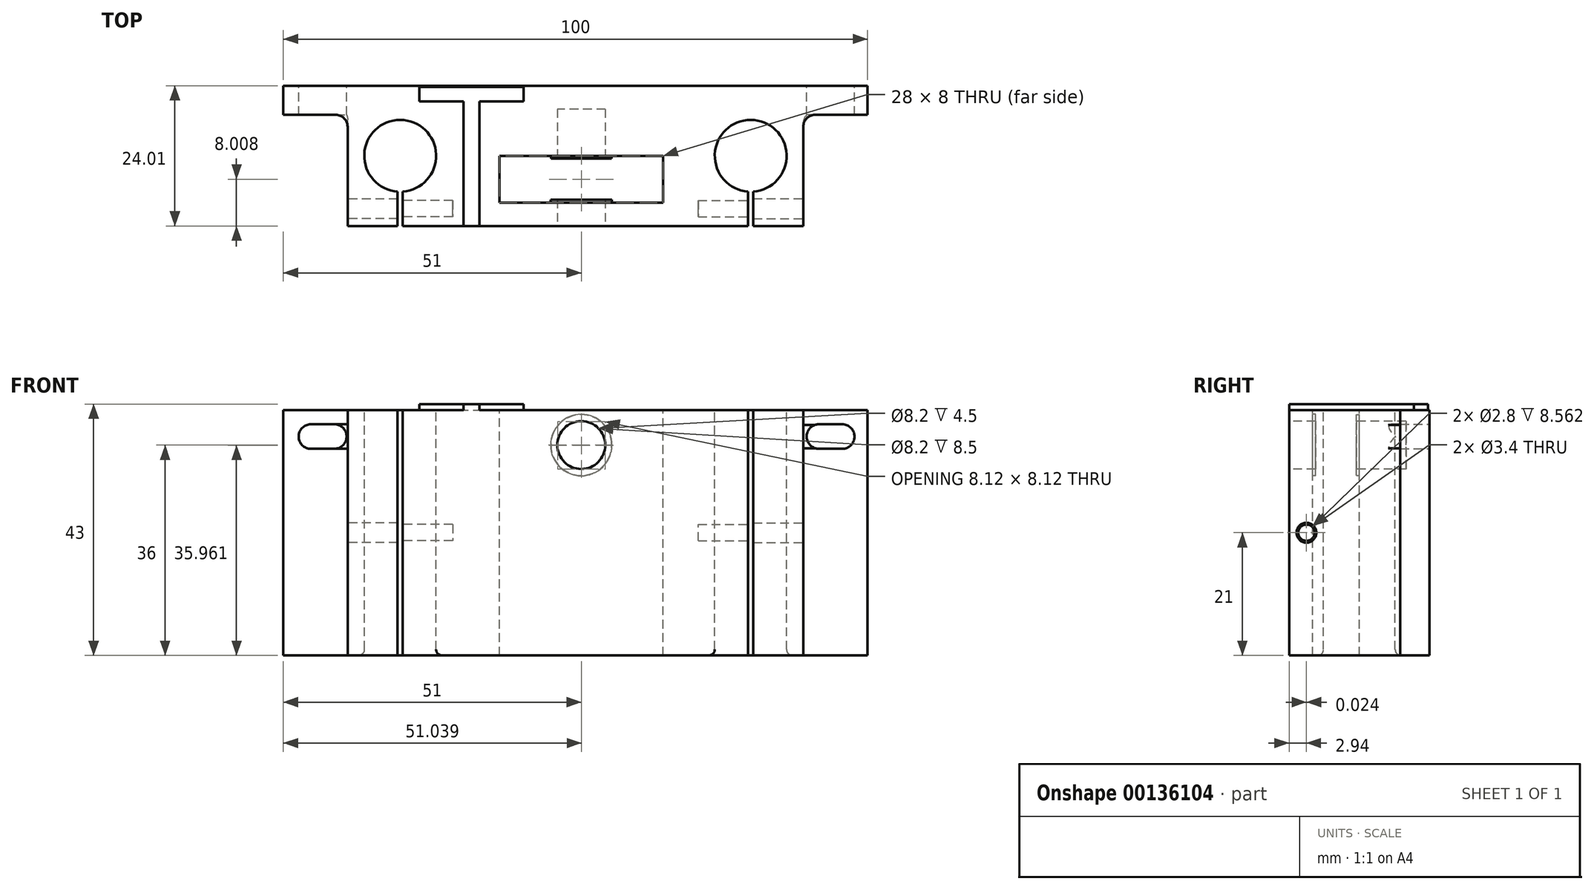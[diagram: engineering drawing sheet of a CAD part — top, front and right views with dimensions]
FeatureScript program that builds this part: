
annotation { "Feature Type Name" : "Feature", "Feature Type Description" : "" }
export const myFeature = defineFeature(function(context is Context, id is Id, definition is map)
    precondition{}
    {
        {
            var Q0;
            Q0=qCreatedBy(makeId("Top.planeOp"),FACE);
            var sketch = newSketch(context, id + "F0", { "sketchPlane" : qUnion([Q0])});
            skLineSegment(sketch, "E0", {"start": v(-46.35, 12.3) * mm, "end": v(53.65, 12.3) * mm});
            skLineSegment(sketch, "E1", {"start": v(53.65, 12.3) * mm, "end": v(53.65, 7.3) * mm});
            skLineSegment(sketch, "E2", {"start": v(53.65, 7.3) * mm, "end": v(42.65, 7.3) * mm});
            skLineSegment(sketch, "E3", {"start": v(42.65, 7.3) * mm, "end": v(42.65, -11.7) * mm});
            skLineSegment(sketch, "E4", {"start": v(42.65, -11.7) * mm, "end": v(-35.35, -11.7) * mm});
            skLineSegment(sketch, "E5", {"start": v(-35.35, -11.7) * mm, "end": v(-35.35, 7.3) * mm});
            skLineSegment(sketch, "E6", {"start": v(-35.35, 7.3) * mm, "end": v(-46.35, 7.3) * mm});
            skLineSegment(sketch, "E7", {"start": v(-46.35, 7.3) * mm, "end": v(-46.35, 12.3) * mm});
            skSolve(sketch);
        }
        {
            var Q0;
            Q0=qSketchRegion(id+"F0",true);
            extrude(context, id + "F1", {"entities" : qUnion([Q0]), "depth" : 12 * mm});
        }
        {
            var Q0;
            Q0=makeQuery(id+"F1.opExtrude","CAP_FACE",FACE,{"disambiguationData":[OSD([sQuery(id+"F0.wireOp",EDGE,"E0"),sQuery(id+"F0.wireOp",EDGE,"E1"),sQuery(id+"F0.wireOp",EDGE,"E2"),sQuery(id+"F0.wireOp",EDGE,"E3"),sQuery(id+"F0.wireOp",EDGE,"E4"),sQuery(id+"F0.wireOp",EDGE,"E5"),sQuery(id+"F0.wireOp",EDGE,"E6"),sQuery(id+"F0.wireOp",EDGE,"E7")])],"isStart":false});
            var sketch = newSketch(context, id + "F2", { "sketchPlane" : qUnion([Q0])});
            skCircle(sketch, "E8", {"center": v(-26.35, 0.3) * mm, "radius": 6.15 * mm});
            skCircle(sketch, "E9", {"center": v(33.65, 0.3) * mm, "radius": 6.15 * mm});
            skPoint(sketch, "E10", {"position": v(3.65, 12.3) * mm});
            skLineSegment(sketch, "E11.bottom", {"start": v(33.21, -3.01) * mm, "end": v(34.09, -3.01) * mm});
            skLineSegment(sketch, "E11.top", {"start": v(33.21, -12.27) * mm, "end": v(34.09, -12.27) * mm});
            skLineSegment(sketch, "E11.left", {"start": v(33.21, -3.01) * mm, "end": v(33.21, -12.27) * mm});
            skLineSegment(sketch, "E11.right", {"start": v(34.09, -3.01) * mm, "end": v(34.09, -12.27) * mm});
            skPoint(sketch, "E12", {"position": v(33.65, -3.01) * mm});
            skLineSegment(sketch, "E13", {"start": v(3.65, 12.3) * mm, "end": v(3.65, -11.7) * mm, "construction": true});
            skLineSegment(sketch, "E14.MirrorCS", {"start": v(-25.91, -12.27) * mm, "end": v(-26.79, -12.27) * mm});
            skLineSegment(sketch, "E15.MirrorCS", {"start": v(-26.79, -3.01) * mm, "end": v(-26.79, -12.27) * mm});
            skLineSegment(sketch, "E16.MirrorCS", {"start": v(-25.91, -3.01) * mm, "end": v(-26.79, -3.01) * mm});
            skLineSegment(sketch, "E17.MirrorCS", {"start": v(-25.91, -3.01) * mm, "end": v(-25.91, -12.27) * mm});
            skSolve(sketch);
        }
        {
            var Q0;
            Q0=qSketchRegion(id+"F2",true);
            var Q1;
            {var subQ3=sQuery(id+"F2.wireOp",EDGE,"E11.bottom");Q1=makeQuery(id+"F2.imprint","IMPRINT",FACE,{"disambiguationData":[TD([[makeQuery(id+"F2.imprint","IMPRINT",EDGE,{"derivedFrom":subQ3}),-1.0]])]});}
            var Q2;
            {var subQ3=sQuery(id+"F2.wireOp",EDGE,"E16.MirrorCS");Q2=makeQuery(id+"F2.imprint","IMPRINT",FACE,{"disambiguationData":[TD([[makeQuery(id+"F2.imprint","IMPRINT",EDGE,{"derivedFrom":subQ3}),1.0]])]});}
            extrude(context, id + "F3", {"entities" : qUnion([Q0, Q1, Q2]), "operationType" : NewBodyOperationType.REMOVE, "endBound" : BoundingType.THROUGH_ALL, "oppositeDirection" : true, "depth" : 25 * mm});
        }
        {
            var Q0;
            Q0=makeQuery(id+"F1.opExtrude","SWEPT_FACE",FACE,{"disambiguationData":[OSD([sQuery(id+"F0.wireOp",EDGE,"E0")])]});
            var sketch = newSketch(context, id + "F4", { "sketchPlane" : qUnion([Q0])});
            skLineSegment(sketch, "E18", {"start": v(-53.65, 7.46) * mm, "end": v(46.35, 7.46) * mm, "construction": true});
            skLineSegment(sketch, "E19.bottom", {"start": v(-49.32, 9.56) * mm, "end": v(-45.32, 9.56) * mm});
            skLineSegment(sketch, "E19.top", {"start": v(-49.32, 5.36) * mm, "end": v(-45.32, 5.36) * mm});
            skArc(sketch, "E20", {"start": v(-45.32, 5.36) * mm, "mid": v(-43.22, 7.46) * mm, "end": v(-45.32, 9.56) * mm});
            skArc(sketch, "E21", {"start": v(-49.32, 9.56) * mm, "mid": v(-51.42, 7.46) * mm, "end": v(-49.32, 5.36) * mm});
            skLineSegment(sketch, "E22.top", {"start": v(37.62, 5.36) * mm, "end": v(41.62, 5.36) * mm});
            skLineSegment(sketch, "E22.bottom", {"start": v(37.62, 9.56) * mm, "end": v(41.62, 9.56) * mm});
            skArc(sketch, "E23", {"start": v(37.62, 9.56) * mm, "mid": v(35.52, 7.46) * mm, "end": v(37.62, 5.36) * mm});
            skArc(sketch, "E24", {"start": v(41.62, 5.36) * mm, "mid": v(43.72, 7.46) * mm, "end": v(41.62, 9.56) * mm});
            skSolve(sketch);
        }
        {
            var Q0;
            Q0=qSketchRegion(id+"F4",true);
            extrude(context, id + "F5", {"entities" : qUnion([Q0]), "operationType" : NewBodyOperationType.REMOVE, "endBound" : BoundingType.THROUGH_ALL, "oppositeDirection" : true, "depth" : 25 * mm});
        }
        {
            var Q0;
            Q0=makeQuery(id+"F1.opExtrude","SWEPT_FACE",FACE,{"disambiguationData":[OSD([sQuery(id+"F0.wireOp",EDGE,"E4")])]});
            var sketch = newSketch(context, id + "F6", { "sketchPlane" : qUnion([Q0])});
            skLineSegment(sketch, "E25", {"start": v(-35.35, 6) * mm, "end": v(42.65, 6) * mm, "construction": true});
            skCircle(sketch, "E26", {"center": v(4.65, 6) * mm, "radius": 4.1 * mm});
            skSolve(sketch);
        }
        {
            var Q0;
            Q0=qSketchRegion(id+"F6",true);
            extrude(context, id + "F7", {"entities" : qUnion([Q0]), "operationType" : NewBodyOperationType.REMOVE, "oppositeDirection" : true, "depth" : 20 * mm});
        }
        {
            var Q0;
            Q0=makeQuery(id+"F1.opExtrude","CAP_FACE",FACE,{"disambiguationData":[OSD([sQuery(id+"F0.wireOp",EDGE,"E0"),sQuery(id+"F0.wireOp",EDGE,"E1"),sQuery(id+"F0.wireOp",EDGE,"E2"),sQuery(id+"F0.wireOp",EDGE,"E3"),sQuery(id+"F0.wireOp",EDGE,"E4"),sQuery(id+"F0.wireOp",EDGE,"E5"),sQuery(id+"F0.wireOp",EDGE,"E6"),sQuery(id+"F0.wireOp",EDGE,"E7")])],"isStart":false});
            var sketch = newSketch(context, id + "F8", { "sketchPlane" : qUnion([Q0])});
            skLineSegment(sketch, "E27.bottom", {"start": v(-9.35, 0.3) * mm, "end": v(18.65, 0.3) * mm});
            skLineSegment(sketch, "E27.top", {"start": v(-9.35, -7.7) * mm, "end": v(18.65, -7.7) * mm});
            skLineSegment(sketch, "E27.left", {"start": v(-9.35, 0.3) * mm, "end": v(-9.35, -7.7) * mm});
            skLineSegment(sketch, "E27.right", {"start": v(18.65, 0.3) * mm, "end": v(18.65, -7.7) * mm});
            skLineSegment(sketch, "E28", {"start": v(4.65, 12.3) * mm, "end": v(4.65, -11.7) * mm, "construction": true});
            skLineSegment(sketch, "E29", {"start": v(4.65, 0.3) * mm, "end": v(4.65, -7.7) * mm});
            skSolve(sketch);
        }
        {
            var Q0;
            Q0=qSketchRegion(id+"F8",true);
            extrude(context, id + "F9", {"entities" : qUnion([Q0]), "operationType" : NewBodyOperationType.REMOVE, "endBound" : BoundingType.THROUGH_ALL, "oppositeDirection" : true, "depth" : 25 * mm});
        }
        {
            var Q0;
            Q0=makeQuery(id+"F9.boolean.opBoolean","COPY",FACE,{"derivedFrom":makeQuery(id+"F9.opExtrude","SWEPT_FACE",FACE,{"disambiguationData":[OSD([sQuery(id+"F8.wireOp",EDGE,"E27.bottom")])]})});
            var sketch = newSketch(context, id + "F10", { "sketchPlane" : qUnion([Q0])});
            skCircle(sketch, "E30", {"center": v(4.65, 6) * mm, "radius": 5.2 * mm});
            skSolve(sketch);
        }
        {
            var Q0;
            Q0=makeQuery(id+"F10.imprint","IMPRINT",FACE,{"disambiguationData":[TD([[makeQuery(id+"F10.imprint","IMPRINT",EDGE,{"derivedFrom":sQuery(id+"F10.wireOp",EDGE,"E30")}),1.0]])]});
            extrude(context, id + "F11", {"entities" : qUnion([Q0]), "operationType" : NewBodyOperationType.ADD, "depth" : 0.5 * mm});
        }
        {
            var Q0;
            Q0=makeQuery(id+"F9.boolean.opBoolean","COPY",FACE,{"derivedFrom":makeQuery(id+"F9.opExtrude","SWEPT_FACE",FACE,{"disambiguationData":[OSD([sQuery(id+"F8.wireOp",EDGE,"E27.top")])]})});
            var sketch = newSketch(context, id + "F12", { "sketchPlane" : qUnion([Q0])});
            skCircle(sketch, "E31", {"center": v(-4.65, 6) * mm, "radius": 5.25 * mm});
            skSolve(sketch);
        }
        {
            var Q0;
            Q0=makeQuery(id+"F12.imprint","IMPRINT",FACE,{"disambiguationData":[TD([[makeQuery(id+"F12.imprint","IMPRINT",EDGE,{"derivedFrom":sQuery(id+"F12.wireOp",EDGE,"E31")}),1.0]])]});
            extrude(context, id + "F13", {"entities" : qUnion([Q0]), "operationType" : NewBodyOperationType.ADD, "depth" : 0.5 * mm});
        }
        {
            var Q0;
            Q0=makeQuery(id+"F1.opExtrude","CAP_FACE",FACE,{"disambiguationData":[OSD([sQuery(id+"F0.wireOp",EDGE,"E0"),sQuery(id+"F0.wireOp",EDGE,"E1"),sQuery(id+"F0.wireOp",EDGE,"E2"),sQuery(id+"F0.wireOp",EDGE,"E3"),sQuery(id+"F0.wireOp",EDGE,"E4"),sQuery(id+"F0.wireOp",EDGE,"E5"),sQuery(id+"F0.wireOp",EDGE,"E6"),sQuery(id+"F0.wireOp",EDGE,"E7")])],"isStart":false});
            var sketch = newSketch(context, id + "F14", { "sketchPlane" : qUnion([Q0])});
            skText(sketch, "E32", { "text": "T", "fontName": "OpenSans-Regular.ttf"});
            const initialGuessF14  = {"E32": [-0.02337, -0.0117, 1, 0, 0.024]};
            skSetInitialGuess(sketch, initialGuessF14);
            skSolve(sketch);
        }
        {
            var Q0;
            Q0=qSketchRegion(id+"F14",true);
            extrude(context, id + "F15", {"entities" : qUnion([Q0]), "operationType" : NewBodyOperationType.ADD, "depth" : 1 * mm});
        }
        {
            var Q0;
            Q0=makeQuery(id+"F1.opExtrude","SWEPT_EDGE",EDGE,{"disambiguationData":[OSD([sQuery(id+"F0.wireOp",EDGE,"E2"),sQuery(id+"F0.wireOp",EDGE,"E3")])]});
            fillet(context, id + "F16", {"entities" : qUnion([Q0]), "radius" : 2 * mm, "tangentPropagation" : true, "allowEdgeOverflow" : false});
        }
        {
            var Q0;
            Q0=makeQuery(id+"F1.opExtrude","SWEPT_EDGE",EDGE,{"disambiguationData":[OSD([sQuery(id+"F0.wireOp",EDGE,"E5"),sQuery(id+"F0.wireOp",EDGE,"E6")])]});
            fillet(context, id + "F17", {"entities" : qUnion([Q0]), "radius" : 2 * mm, "tangentPropagation" : true, "allowEdgeOverflow" : false});
        }
        {
            var Q0;
            Q0=makeQuery(id+"F1.opExtrude","CAP_FACE",FACE,{"disambiguationData":[OSD([sQuery(id+"F0.wireOp",EDGE,"E0"),sQuery(id+"F0.wireOp",EDGE,"E1"),sQuery(id+"F0.wireOp",EDGE,"E2"),sQuery(id+"F0.wireOp",EDGE,"E3"),sQuery(id+"F0.wireOp",EDGE,"E4"),sQuery(id+"F0.wireOp",EDGE,"E5"),sQuery(id+"F0.wireOp",EDGE,"E6"),sQuery(id+"F0.wireOp",EDGE,"E7")])],"isStart":true});
            extrude(context, id + "F18", {"entities" : qUnion([Q0]), "operationType" : NewBodyOperationType.ADD, "flatOperationType" : FlatOperationType.REMOVE, "offsetDistance" : 25 * mm, "depth" : 30 * mm, "domain" : OperationDomain.MODEL});
        }
        {
            var Q0;
            Q0=makeQuery(id+"F1.opExtrude","SWEPT_FACE",FACE,{"disambiguationData":[OSD([sQuery(id+"F0.wireOp",EDGE,"E3")])]});
            var sketch = newSketch(context, id + "F19", { "sketchPlane" : qUnion([Q0])});
            skCircle(sketch, "E33", {"center": v(-8.74, -9) * mm, "radius": 1.7 * mm});
            skCircle(sketch, "E34", {"center": v(-8.74, -9) * mm, "radius": 1.4 * mm});
            skLineSegment(sketch, "E35", {"start": v(-11.7, -9) * mm, "end": v(-3.84, -9) * mm, "construction": true});
            skSolve(sketch);
        }
        {
            var Q0;
            Q0=makeQuery(id+"F19.imprint","IMPRINT",FACE,{"disambiguationData":[TD([[makeQuery(id+"F19.imprint","IMPRINT",EDGE,{"derivedFrom":sQuery(id+"F19.wireOp",EDGE,"E34")}),1.0]])]});
            extrude(context, id + "F20", {"entities" : qUnion([Q0]), "operationType" : NewBodyOperationType.REMOVE, "oppositeDirection" : true, "depth" : 18 * mm});
        }
        {
            var Q0;
            Q0=makeQuery(id+"F19.imprint","IMPRINT",FACE,{"disambiguationData":[TD([[makeQuery(id+"F19.imprint","IMPRINT",EDGE,{"derivedFrom":sQuery(id+"F19.wireOp",EDGE,"E34")}),1.0]])]});
            var Q1;
            Q1=makeQuery(id+"F19.imprint","IMPRINT",FACE,{"disambiguationData":[TD([[makeQuery(id+"F19.imprint","IMPRINT",EDGE,{"derivedFrom":sQuery(id+"F19.wireOp",EDGE,"E33")}),1.0]])]});
            extrude(context, id + "F21", {"entities" : qUnion([Q0, Q1]), "operationType" : NewBodyOperationType.REMOVE, "endBound" : BoundingType.UP_TO_NEXT, "oppositeDirection" : true, "depth" : 7 * mm});
        }
        {
            var Q0;
            Q0=makeQuery(id+"F1.opExtrude","SWEPT_FACE",FACE,{"disambiguationData":[OSD([sQuery(id+"F0.wireOp",EDGE,"E5")])]});
            var sketch = newSketch(context, id + "F22", { "sketchPlane" : qUnion([Q0])});
            skCircle(sketch, "E36", {"center": v(8.76, -9) * mm, "radius": 1.7 * mm});
            skCircle(sketch, "E37", {"center": v(8.76, -9) * mm, "radius": 1.4 * mm});
            skLineSegment(sketch, "E38", {"start": v(8.76, -30) * mm, "end": v(8.76, 12) * mm, "construction": true});
            skSolve(sketch);
        }
        {
            var Q0;
            Q0=makeQuery(id+"F22.imprint","IMPRINT",FACE,{"disambiguationData":[TD([[makeQuery(id+"F22.imprint","IMPRINT",EDGE,{"derivedFrom":sQuery(id+"F22.wireOp",EDGE,"E37")}),1.0]])]});
            extrude(context, id + "F23", {"entities" : qUnion([Q0]), "operationType" : NewBodyOperationType.REMOVE, "oppositeDirection" : true, "depth" : 18 * mm});
        }
        {
            var Q0;
            Q0=makeQuery(id+"F22.imprint","IMPRINT",FACE,{"disambiguationData":[TD([[makeQuery(id+"F22.imprint","IMPRINT",EDGE,{"derivedFrom":sQuery(id+"F22.wireOp",EDGE,"E37")}),1.0]])]});
            var Q1;
            Q1=makeQuery(id+"F22.imprint","IMPRINT",FACE,{"disambiguationData":[TD([[makeQuery(id+"F22.imprint","IMPRINT",EDGE,{"derivedFrom":sQuery(id+"F22.wireOp",EDGE,"E36")}),1.0]])]});
            extrude(context, id + "F24", {"entities" : qUnion([Q0, Q1]), "operationType" : NewBodyOperationType.REMOVE, "endBound" : BoundingType.UP_TO_NEXT, "oppositeDirection" : true, "depth" : 25 * mm});
        }
        {
            var Q0;
            Q0=makeQuery(id+"F18.opExtrude","CAP_EDGE",EDGE,{"disambiguationData":[OSD([sQuery(id+"F0.wireOp",EDGE,"E0"),sQuery(id+"F0.wireOp",EDGE,"E1"),sQuery(id+"F0.wireOp",EDGE,"E2"),sQuery(id+"F0.wireOp",EDGE,"E3"),sQuery(id+"F0.wireOp",EDGE,"E4"),sQuery(id+"F0.wireOp",EDGE,"E5"),sQuery(id+"F0.wireOp",EDGE,"E6"),sQuery(id+"F0.wireOp",EDGE,"E7"),sQuery(id+"F2.wireOp",EDGE,"E9")])],"isStart":false});
            var Q1;
            Q1=makeQuery(id+"F18.opExtrude","CAP_EDGE",EDGE,{"disambiguationData":[OSD([sQuery(id+"F0.wireOp",EDGE,"E0"),sQuery(id+"F0.wireOp",EDGE,"E1"),sQuery(id+"F0.wireOp",EDGE,"E2"),sQuery(id+"F0.wireOp",EDGE,"E3"),sQuery(id+"F0.wireOp",EDGE,"E4"),sQuery(id+"F0.wireOp",EDGE,"E5"),sQuery(id+"F0.wireOp",EDGE,"E6"),sQuery(id+"F0.wireOp",EDGE,"E7"),sQuery(id+"F2.wireOp",EDGE,"E8")])],"isStart":false});
            fillet(context, id + "F25", {"entities" : qUnion([Q0, Q1]), "radius" : 1 * mm, "tangentPropagation" : true, "allowEdgeOverflow" : false});
        }
    });
